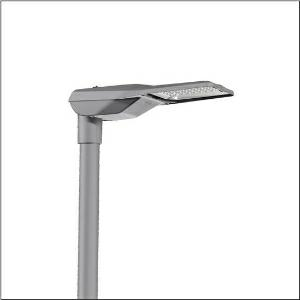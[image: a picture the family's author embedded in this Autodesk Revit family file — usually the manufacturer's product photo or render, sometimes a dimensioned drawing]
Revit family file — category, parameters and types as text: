
# Revit family: streetlight_sl_21_mini___pl52_5xe2h33s08gb_224a
name_source: partatom
category: Lighting Fixtures
units: mm (PartAtom-declared; Revit-internal decimal feet)

## family parameters
Cut with Voids When Loaded = No
Host = Face
Light Source = No
Part Type = Normal
Room Calculation Point = No
Round Connector Dimension = Use Diameter
Shared = No

## types (1)
- --- (1 x LED, 5840 lm, 40.4 W, 3000K)
    Apparent Load = 40 VA
    CIE Flux Codes = 27 59 98 100 100
    Color Rendering = 70
    Color Temperature = 3000K
    Default Elevation = 1800 mm
    Description = Streetlight SL 21 mini, mast luminaire, primary light control with lens, of PMMA, primary optical cover: cover, of toughened safety glass, transparent, light distribution: PL52, light emission: direct distribution, primary light characteristic: asymmetric, installation type: side-entry, post-top, LED, High Power LED, rated luminous flux: 5.840lm, luminous efficacy: 144lm/W, light colour: 730, colour temperature: 3000K, control gear: ECG Smart Interface, control: overheat protection, constant luminous flux control, time-dependent luminous flux control, flexible luminous flux parameterisation, mains connection: 220..240V, AC, 50/60Hz, start of lifetime: 40W, end of lifetime: 41W, reduction: 19W, luminaire housing, of diecast aluminium, powder-coated, Siteco® metallic grey (DB 702S), corrosivity category C5 according to DIN EN ISO 12944, length: 628mm, width: 235mm, height: 110mm, spigot size: 60/76mm (post-top) and 42/60/76mm (side-entry), mast flange for spigot size: 42mm: 5XC10008XM4, 60mm: 5XC10008XM2, 76/60mm: 5XC10108XM1, protection rating (complete): IP66, insulation class (complete): insulation class II (safety insulation), certification: CE, ENEC, VDE, impact resistance: IK09, permissible operating ambient temperature for outdoor applications: -40..+50°C, standard-compliant lighting for roads and squares, packaging unit: 1 piece

Light Distribution: PL52
    Height = 110 mm
    Lamp = 1 x LED
    Lamp Light Flux = 5840 lm
    Lamp Power = 40.4 W
    Lamp count = 1
    Length = 625 mm
    Luminous efficacy = 145 lm/W
    Manufacturer = Siteco
    ModVariant = No
    Model = 5XE2H33S08GB
    Number of Poles = 1
    OnlyDefault = Yes
    Power Factor = 1
    Product Name = Streetlight SL 21 mini | PL52
    Product group = mast luminaire | pylon top
    ProductGroupID = 6100
    Protection Class = Protection class II
    Protection Degree = IP 66
    RLX_Detail_Level = 1
    RlxData = <blob elided: 101401 chars, md5=98d6e08b>
    Socket = socket
    Standby Power = 0 W
    System Light Flux = 5840 lm
    System Power = 40 W
    Type Comments = factory setting: luminous flux: 100 % | dim-lin: 254 | 812 mA
    Type Image = l_1003515.jpg
    URL = http://relux.com
    VarID = @adj_109417
    Voltage = 0 V
    Weight = 0.00 kg
    Width = 234 mm

## geometry (parser evidence)
native form markers: Blend x4, Sweep x10
no freeform markers — native parametric forms only
